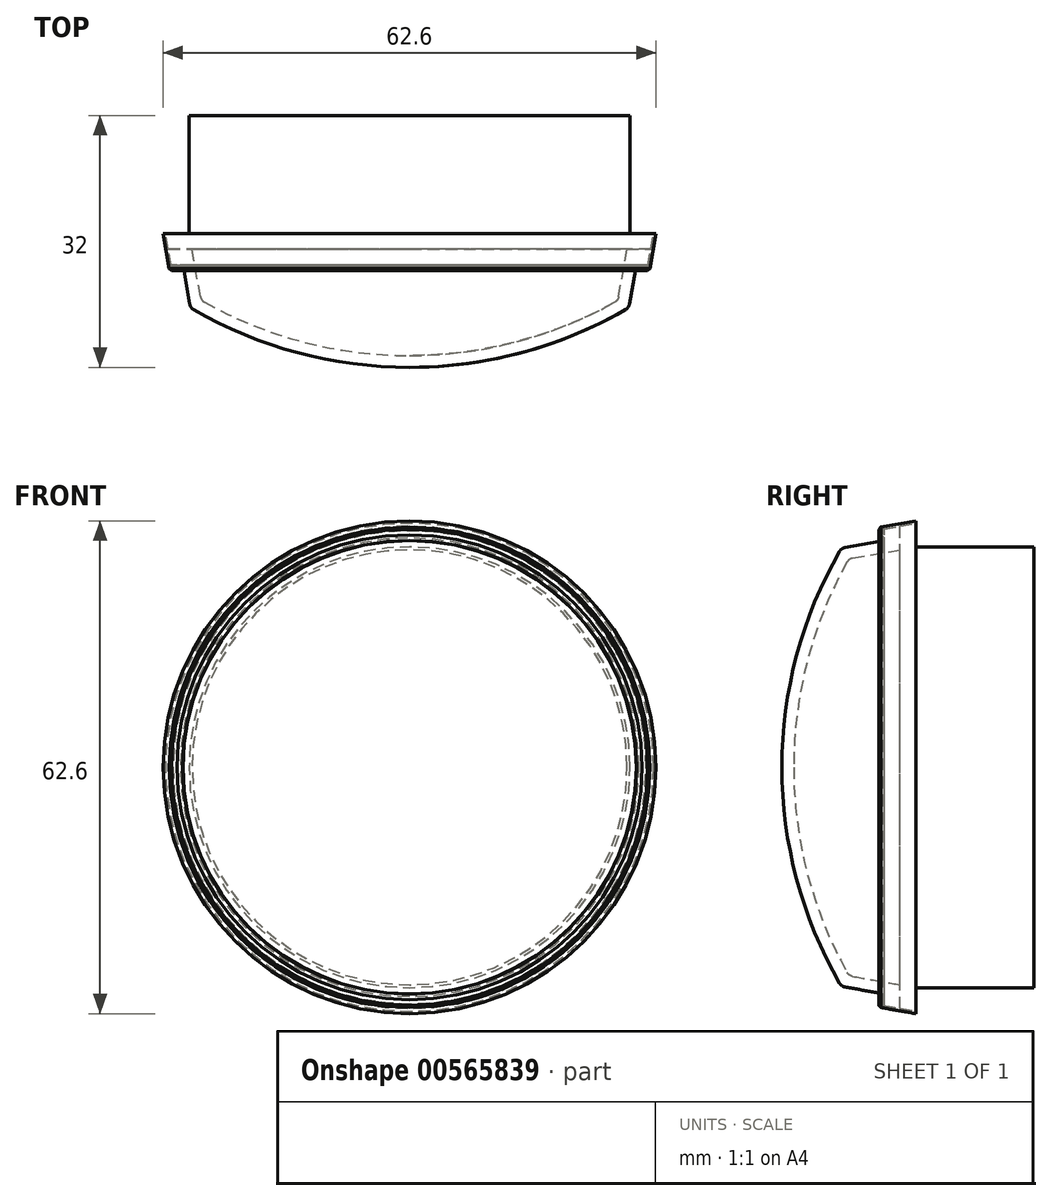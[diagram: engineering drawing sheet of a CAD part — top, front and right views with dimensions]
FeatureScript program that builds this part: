
annotation { "Feature Type Name" : "Feature", "Feature Type Description" : "" }
export const myFeature = defineFeature(function(context is Context, id is Id, definition is map)
    precondition{}
    {
        {
            var Q0;
            Q0=qCreatedBy(makeId("Front.planeOp"),FACE);
            var sketch = newSketch(context, id + "F0", { "sketchPlane" : qUnion([Q0])});
            skCircle(sketch, "E0", {"center": v(0, 0) * mm, "radius": 28 * mm});
            skSolve(sketch);
        }
        {
            var Q0;
            Q0=makeQuery(id+"F0.imprint","IMPRINT",FACE,{"disambiguationData":[TD([[makeQuery(id+"F0.imprint","IMPRINT",EDGE,{"derivedFrom":sQuery(id+"F0.wireOp",EDGE,"E0")}),1.0]])]});
            extrude(context, id + "F1", {"entities" : qUnion([Q0]), "depth" : 15 * mm, "offsetDistance" : 25 * mm});
        }
        {
            var Q0;
            Q0=qCreatedBy(makeId("Top.planeOp"),FACE);
            var sketch = newSketch(context, id + "F2", { "sketchPlane" : qUnion([Q0])});
            skLineSegment(sketch, "E1", {"start": v(0, -15) * mm, "end": v(31, -15) * mm});
            skLineSegment(sketch, "E2", {"start": v(31, -15) * mm, "end": v(30.65, -17) * mm});
            skLineSegment(sketch, "E3", {"start": v(30.65, -17) * mm, "end": v(0, -17) * mm});
            skLineSegment(sketch, "E4", {"start": v(0, -17) * mm, "end": v(0, -15) * mm});
            skLineSegment(sketch, "E5", {"start": v(28, 0) * mm, "end": v(28, -15) * mm});
            skLineSegment(sketch, "E6", {"start": v(0, -15) * mm, "end": v(0, 0) * mm, "construction": true});
            skSolve(sketch);
        }
        {
            var Q0;
            {var subQ0=sQuery(id+"F2.wireOp",EDGE,"E2");Q0=makeQuery(id+"F2.imprint","IMPRINT",FACE,{"disambiguationData":[TD([[makeQuery(id+"F2.imprint","IMPRINT",EDGE,{"derivedFrom":subQ0}),-1.0]])]});}
            var Q1;
            Q1=sQuery(id+"F2.wireOp",EDGE,"E6");
            revolve(context, id + "F3", {"operationType" : NewBodyOperationType.ADD, "entities" : qUnion([Q0]), "axis" : qUnion([Q1]), "revolveType" : RevolveType.FULL});
        }
        {
            var Q0;
            Q0=qCreatedBy(makeId("Top.planeOp"),FACE);
            var sketch = newSketch(context, id + "F4", { "sketchPlane" : qUnion([Q0])});
            skLineSegment(sketch, "E7", {"start": v(30.65, -17) * mm, "end": v(30.3, -19) * mm});
            skLineSegment(sketch, "E8", {"start": v(30.3, -19) * mm, "end": v(28.8, -19) * mm});
            skLineSegment(sketch, "E9", {"start": v(28.8, -19) * mm, "end": v(27.92, -23.98) * mm});
            skLineSegment(sketch, "E10", {"start": v(30.65, -17) * mm, "end": v(27.62, -17) * mm});
            skLineSegment(sketch, "E11", {"start": v(27.62, -17) * mm, "end": v(26.56, -23.02) * mm});
            skArc(sketch, "E12", {"start": v(0, -32) * mm, "mid": v(14.2, -30.14) * mm, "end": v(27.43, -24.67) * mm});
            skArc(sketch, "E13", {"start": v(0, -30.5) * mm, "mid": v(13.47, -28.78) * mm, "end": v(26.06, -23.72) * mm});
            skLineSegment(sketch, "E14", {"start": v(0, -32) * mm, "end": v(0, -30.5) * mm});
            skPoint(sketch, "E15.visualSharp", {"position": v(27.84, -24.44) * mm});
            skArc(sketch, "E15.filletArc", {"start": v(27.43, -24.67) * mm, "mid": v(27.75, -24.38) * mm, "end": v(27.92, -23.98) * mm});
            skPoint(sketch, "E16.visualSharp", {"position": v(26.48, -23.49) * mm});
            skArc(sketch, "E16.filletArc", {"start": v(26.06, -23.72) * mm, "mid": v(26.4, -23.43) * mm, "end": v(26.56, -23.02) * mm});
            skSolve(sketch);
        }
        {
            var Q0;
            Q0=makeQuery(id+"F4.imprint","IMPRINT",FACE,{"disambiguationData":[TD([[makeQuery(id+"F4.imprint","IMPRINT",EDGE,{"derivedFrom":sQuery(id+"F4.wireOp",EDGE,"E7")}),-1.0]])]});
            var Q1;
            Q1=sQuery(id+"F2.wireOp",EDGE,"E6");
            revolve(context, id + "F5", {"entities" : qUnion([Q0]), "axis" : qUnion([Q1]), "revolveType" : RevolveType.FULL});
        }
        {
            var Q0;
            Q0=qCreatedBy(makeId("Top.planeOp"),FACE);
            var sketch = newSketch(context, id + "F6", { "sketchPlane" : qUnion([Q0])});
            skLineSegment(sketch, "E17", {"start": v(30.52, -19.42) * mm, "end": v(31.3, -15) * mm});
            skLineSegment(sketch, "E18", {"start": v(31.3, -15) * mm, "end": v(31, -15) * mm});
            skLineSegment(sketch, "E19", {"start": v(31, -15) * mm, "end": v(30.26, -19.2) * mm});
            skLineSegment(sketch, "E20", {"start": v(31, -15) * mm, "end": v(30.65, -17) * mm});
            skLineSegment(sketch, "E21.0", {"start": v(0, -15) * mm, "end": v(31, -15) * mm});
            skLineSegment(sketch, "E22", {"start": v(31, -15) * mm, "end": v(31, -15) * mm});
            skLineSegment(sketch, "E23", {"start": v(30.26, -19.2) * mm, "end": v(30.05, -19.42) * mm});
            skLineSegment(sketch, "E24", {"start": v(30.05, -19.42) * mm, "end": v(29.55, -19.42) * mm});
            skLineSegment(sketch, "E25", {"start": v(29.55, -19.42) * mm, "end": v(29.13, -19) * mm});
            skLineSegment(sketch, "E26", {"start": v(30.52, -19.42) * mm, "end": v(30.24, -19.7) * mm});
            skLineSegment(sketch, "E27", {"start": v(30.24, -19.7) * mm, "end": v(29.54, -19.7) * mm});
            skLineSegment(sketch, "E28", {"start": v(29.54, -19.7) * mm, "end": v(28.83, -19) * mm});
            skLineSegment(sketch, "E29", {"start": v(28.83, -19) * mm, "end": v(29.13, -19) * mm});
            skSolve(sketch);
        }
        {
            var Q0;
            Q0=makeQuery(id+"F6.imprint","IMPRINT",FACE,{"disambiguationData":[TD([[makeQuery(id+"F6.imprint","IMPRINT",EDGE,{"derivedFrom":sQuery(id+"F6.wireOp",EDGE,"E17")}),1.0]])]});
            var Q1;
            Q1=sQuery(id+"F2.wireOp",EDGE,"E6");
            revolve(context, id + "F7", {"entities" : qUnion([Q0]), "axis" : qUnion([Q1]), "revolveType" : RevolveType.FULL});
        }
    });
